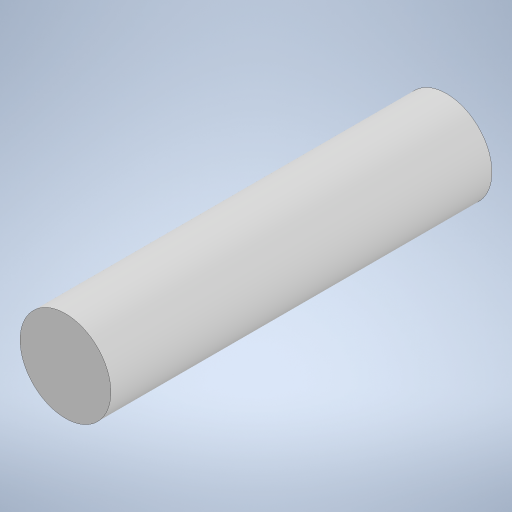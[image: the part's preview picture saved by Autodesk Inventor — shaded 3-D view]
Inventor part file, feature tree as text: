
AUTODESK INVENTOR PART (.ipt)
format: ipt  version: 2023.5 (Build 275446000, 446)  size: 218,112 bytes
history: native  units: in
note: dims shown in document units (in); Inventor stores cm internally (conversion verified against a paired STEP export)
features: extrude x2, sketch x2
ambient origin geometry x8: Origin, YZ Plane, XZ Plane, XY Plane, X Axis, Y Axis, Z Axis, Center Point
bodies: Solid1 (feature_tree)
feature tree (4):
  extrude  "Extrusion1"  Depth=0.4134in TaperAngle=0.0deg
  extrude  "Extrusion2"  Depth=0.2953in TaperAngle=0.0deg
  sketch  "Sketch1"  dims[d0=0.0984in d1=0.4134in d2=0.0in]
  sketch  "Sketch2"  dims[d3=0.0394in d4=0.2953in d5=0.0in d6=0.0197in d7=0.0344in d8=0.0197in d9=0.0344in]
